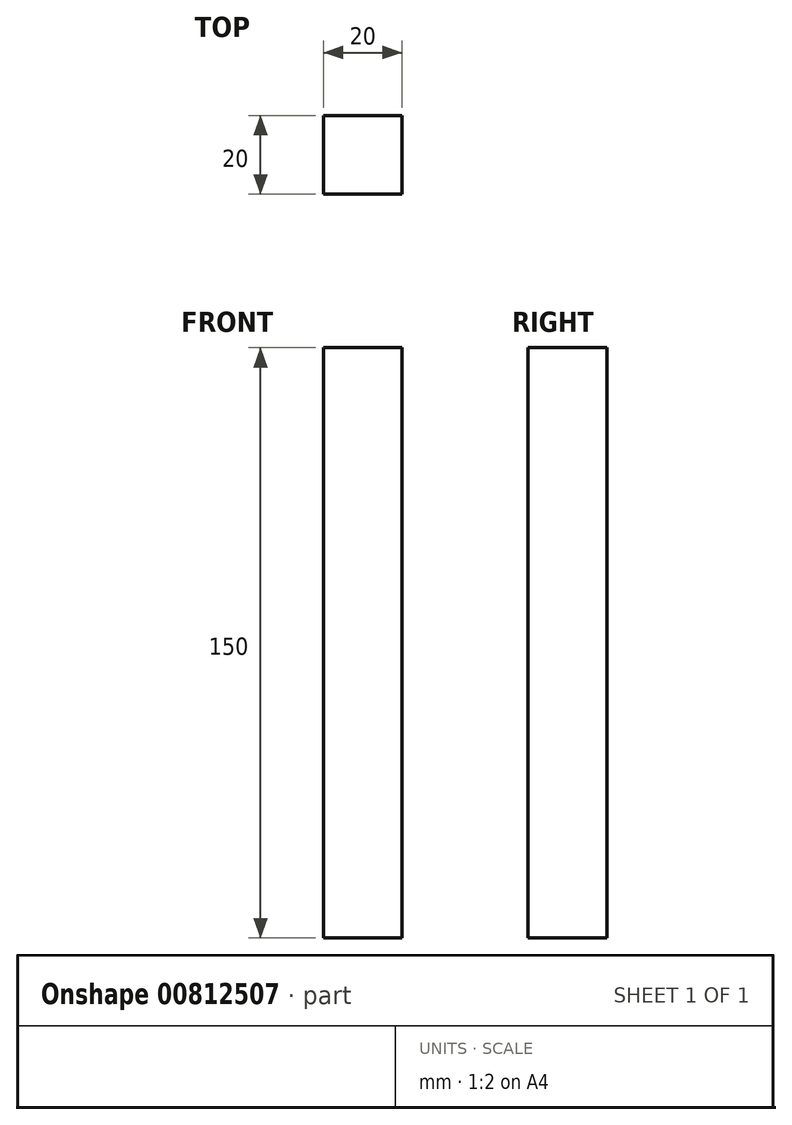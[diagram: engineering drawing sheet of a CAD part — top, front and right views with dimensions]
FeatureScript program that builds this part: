
annotation { "Feature Type Name" : "Feature", "Feature Type Description" : "" }
export const myFeature = defineFeature(function(context is Context, id is Id, definition is map)
    precondition{}
    {
        {
            var Q0;
            Q0=qCreatedBy(makeId("Top.planeOp"),FACE);
            var sketch = newSketch(context, id + "F0", { "sketchPlane" : qUnion([Q0])});
            skLineSegment(sketch, "E0.bottom", {"start": v(10, -10) * mm, "end": v(-10, -10) * mm});
            skLineSegment(sketch, "E0.top", {"start": v(10, 10) * mm, "end": v(-10, 10) * mm});
            skLineSegment(sketch, "E0.left", {"start": v(10, -10) * mm, "end": v(10, 10) * mm});
            skLineSegment(sketch, "E0.right", {"start": v(-10, -10) * mm, "end": v(-10, 10) * mm});
            skPoint(sketch, "E0.middle", {"position": v(0, 0) * mm});
            skSolve(sketch);
        }
        {
            var Q0;
            Q0 = qSketchRegion(id + "F0", true);
            extrude(context, id + "F1", {"entities" : qUnion([Q0]), "depth" : 150 * mm, "offsetDistance" : 25 * mm});
        }
    });
